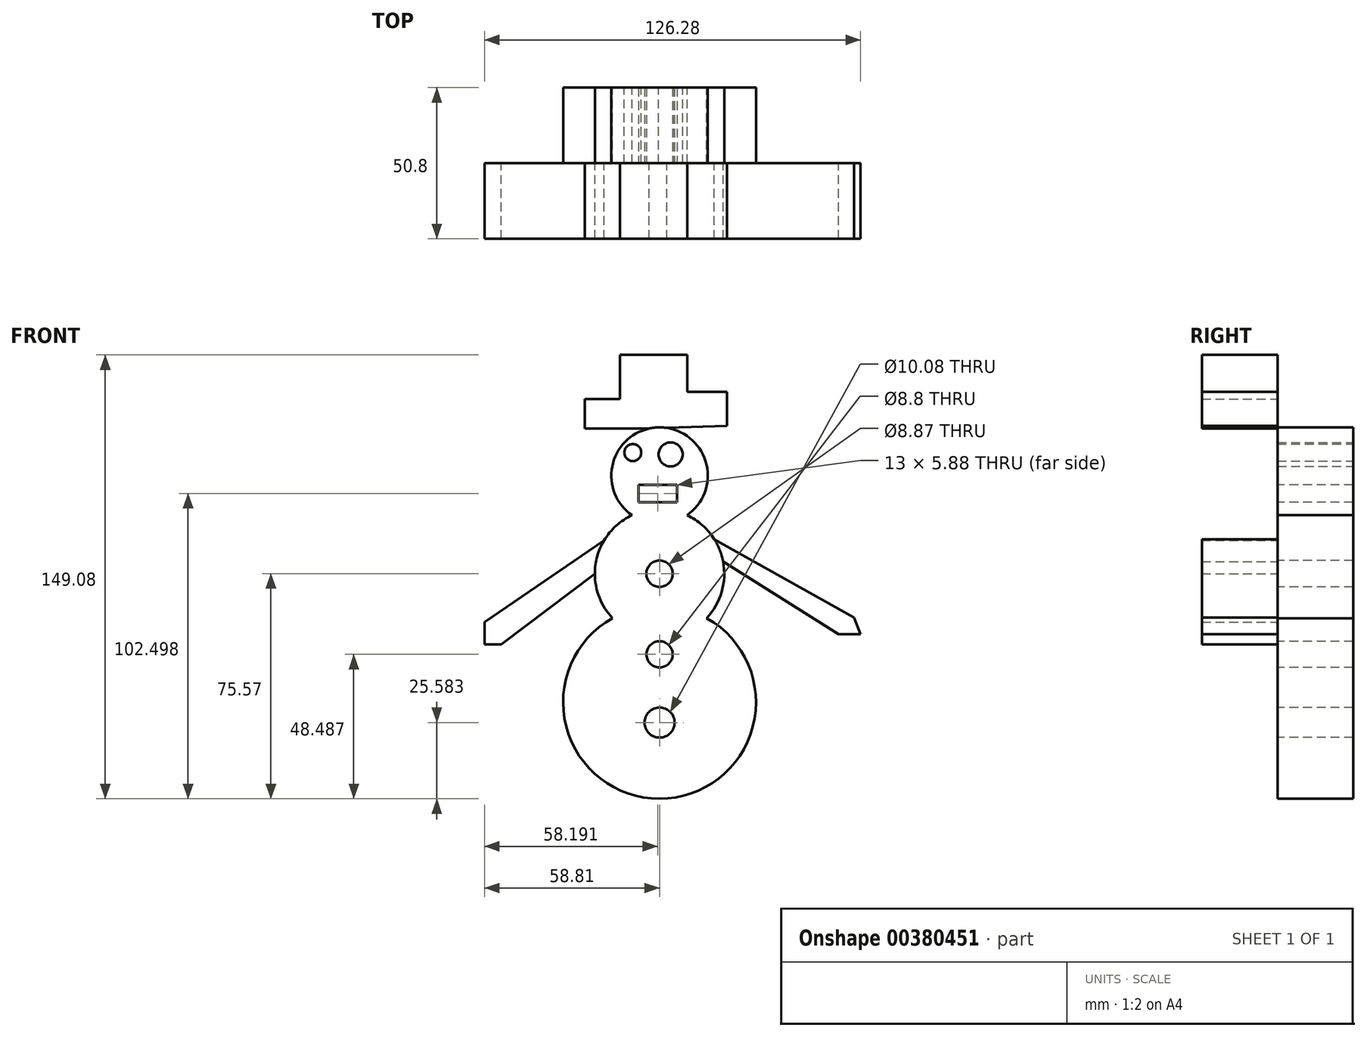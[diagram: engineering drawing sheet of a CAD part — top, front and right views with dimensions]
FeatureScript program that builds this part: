
annotation { "Feature Type Name" : "Feature", "Feature Type Description" : "" }
export const myFeature = defineFeature(function(context is Context, id is Id, definition is map)
    precondition{}
    {
        {
            var Q0;
            Q0=qCreatedBy(makeId("Front.planeOp"),FACE);
            var sketch = newSketch(context, id + "F0", { "sketchPlane" : qUnion([Q0])});
            skCircle(sketch, "E0", {"center": v(0, 0) * mm, "radius": 21.74 * mm});
            skCircle(sketch, "E1", {"center": v(0, -43.18) * mm, "radius": 32.4 * mm});
            skCircle(sketch, "E2", {"center": v(0, 32.96) * mm, "radius": 16.2 * mm});
            skCircle(sketch, "E3", {"center": v(-8.98, 40.7) * mm, "radius": 2.85 * mm});
            skLineSegment(sketch, "E4", {"start": v(-9.9, 28.94) * mm, "end": v(-9.9, 23.37) * mm});
            skLineSegment(sketch, "E5", {"start": v(-9.9, 23.37) * mm, "end": v(8.05, 23.37) * mm});
            skCircle(sketch, "E6", {"center": v(3.71, 40.08) * mm, "radius": 4.04 * mm});
            skLineSegment(sketch, "E7", {"start": v(17.9, 12.33) * mm, "end": v(49.52, -4.49) * mm});
            skLineSegment(sketch, "E8", {"start": v(-18.11, 12.02) * mm, "end": v(-42.4, -4.49) * mm});
            skSolve(sketch);
        }
        {
            var Q0;
            Q0 = qSketchRegion(id + "F0", true);
            extrude(context, id + "F1", {"entities" : qUnion([Q0]), "depth" : 25.4 * mm});
        }
        {
            var Q0;
            Q0=makeQuery(id+"F1.opExtrude","CAP_FACE",FACE,{"disambiguationData":[OSD([sQuery(id+"F0.wireOp",EDGE,"E0"),sQuery(id+"F0.wireOp",EDGE,"E1"),sQuery(id+"F0.wireOp",EDGE,"E2"),sQuery(id+"F0.wireOp",EDGE,"E3"),sQuery(id+"F0.wireOp",EDGE,"E6")])],"isStart":false});
            var sketch = newSketch(context, id + "F2", { "sketchPlane" : qUnion([Q0])});
            skLineSegment(sketch, "E9", {"start": v(-7.12, 29.87) * mm, "end": v(-7.12, 23.99) * mm});
            skLineSegment(sketch, "E10", {"start": v(-7.12, 23.99) * mm, "end": v(5.88, 23.99) * mm});
            skLineSegment(sketch, "E11", {"start": v(5.88, 23.99) * mm, "end": v(5.88, 29.87) * mm});
            skLineSegment(sketch, "E12", {"start": v(5.88, 29.87) * mm, "end": v(-7.12, 29.87) * mm});
            skSolve(sketch);
        }
        {
            var Q0;
            Q0=makeQuery(id+"F2.imprint","IMPRINT",FACE,{"disambiguationData":[TD([[makeQuery(id+"F2.imprint","IMPRINT",EDGE,{"derivedFrom":sQuery(id+"F2.wireOp",EDGE,"E9")}),1.0]])]});
            extrude(context, id + "F3", {"entities" : qUnion([Q0]), "operationType" : NewBodyOperationType.REMOVE, "oppositeDirection" : true, "depth" : 25.4 * mm});
        }
        {
            var Q0;
            Q0=makeQuery(id+"F1.opExtrude","CAP_FACE",FACE,{"disambiguationData":[OSD([sQuery(id+"F0.wireOp",EDGE,"E0"),sQuery(id+"F0.wireOp",EDGE,"E1"),sQuery(id+"F0.wireOp",EDGE,"E2"),sQuery(id+"F0.wireOp",EDGE,"E3"),sQuery(id+"F0.wireOp",EDGE,"E6")])],"isStart":false});
            var sketch = newSketch(context, id + "F4", { "sketchPlane" : qUnion([Q0])});
            skCircle(sketch, "E13", {"center": v(0, 0) * mm, "radius": 4.43 * mm});
            skCircle(sketch, "E14", {"center": v(0, -27.08) * mm, "radius": 4.4 * mm});
            skCircle(sketch, "E15", {"center": v(0, -49.99) * mm, "radius": 5.04 * mm});
            skSolve(sketch);
        }
        {
            var Q0;
            Q0 = qSketchRegion(id + "F4", true);
            extrude(context, id + "F5", {"entities" : qUnion([Q0]), "operationType" : NewBodyOperationType.REMOVE, "oppositeDirection" : true, "depth" : 25.4 * mm});
        }
        {
            var Q0;
            Q0=makeQuery(id+"F1.opExtrude","CAP_FACE",FACE,{"disambiguationData":[OSD([sQuery(id+"F0.wireOp",EDGE,"E0"),sQuery(id+"F0.wireOp",EDGE,"E1"),sQuery(id+"F0.wireOp",EDGE,"E2"),sQuery(id+"F0.wireOp",EDGE,"E3"),sQuery(id+"F0.wireOp",EDGE,"E6")])],"isStart":false});
            var sketch = newSketch(context, id + "F6", { "sketchPlane" : qUnion([Q0])});
            skLineSegment(sketch, "E16", {"start": v(-3.54, 48.77) * mm, "end": v(-25.07, 48.77) * mm});
            skLineSegment(sketch, "E17", {"start": v(-25.07, 48.77) * mm, "end": v(-25.07, 58.65) * mm});
            skLineSegment(sketch, "E18", {"start": v(-25.07, 58.65) * mm, "end": v(-13.3, 58.65) * mm});
            skLineSegment(sketch, "E19", {"start": v(-13.3, 58.65) * mm, "end": v(-13.3, 73.51) * mm});
            skLineSegment(sketch, "E20", {"start": v(-13.3, 73.51) * mm, "end": v(9.25, 73.51) * mm});
            skLineSegment(sketch, "E21", {"start": v(9.25, 73.51) * mm, "end": v(9.25, 61.13) * mm});
            skLineSegment(sketch, "E22", {"start": v(9.25, 61.13) * mm, "end": v(22.6, 61.13) * mm});
            skLineSegment(sketch, "E23", {"start": v(22.6, 61.13) * mm, "end": v(22.6, 49.68) * mm});
            skLineSegment(sketch, "E24", {"start": v(22.6, 49.68) * mm, "end": v(-3.54, 48.77) * mm});
            skSolve(sketch);
        }
        {
            var Q0;
            {var subQ1=sQuery(id+"F6.wireOp",EDGE,"E16");Q0=makeQuery(id+"F6.imprint","IMPRINT",FACE,{"disambiguationData":[TD([[makeQuery(id+"F6.imprint","IMPRINT",EDGE,{"derivedFrom":subQ1}),-1.0]])]});}
            extrude(context, id + "F7", {"entities" : qUnion([Q0]), "depth" : 25.4 * mm});
        }
        {
            var Q0;
            Q0=makeQuery(id+"F1.opExtrude","CAP_FACE",FACE,{"disambiguationData":[OSD([sQuery(id+"F0.wireOp",EDGE,"E0"),sQuery(id+"F0.wireOp",EDGE,"E1"),sQuery(id+"F0.wireOp",EDGE,"E2"),sQuery(id+"F0.wireOp",EDGE,"E3"),sQuery(id+"F0.wireOp",EDGE,"E6")])],"isStart":false});
            var sketch = newSketch(context, id + "F8", { "sketchPlane" : qUnion([Q0])});
            skLineSegment(sketch, "E25", {"start": v(18.39, 11.6) * mm, "end": v(65.3, -14.7) * mm});
            skLineSegment(sketch, "E26", {"start": v(65.3, -14.7) * mm, "end": v(67.47, -20.27) * mm});
            skLineSegment(sketch, "E27", {"start": v(67.47, -20.27) * mm, "end": v(60.05, -20.27) * mm});
            skLineSegment(sketch, "E28", {"start": v(60.05, -20.27) * mm, "end": v(21.36, 4.05) * mm});
            skLineSegment(sketch, "E29", {"start": v(21.36, 4.05) * mm, "end": v(18.39, 11.6) * mm});
            skSolve(sketch);
        }
        {
            var Q0;
            {var subQ1=sQuery(id+"F8.wireOp",EDGE,"E25");Q0=makeQuery(id+"F8.imprint","IMPRINT",FACE,{"disambiguationData":[TD([[makeQuery(id+"F8.imprint","IMPRINT",EDGE,{"derivedFrom":subQ1}),-1.0]])]});}
            extrude(context, id + "F9", {"entities" : qUnion([Q0]), "depth" : 25.4 * mm});
        }
        {
            var Q0;
            Q0=makeQuery(id+"F1.opExtrude","CAP_FACE",FACE,{"disambiguationData":[OSD([sQuery(id+"F0.wireOp",EDGE,"E0"),sQuery(id+"F0.wireOp",EDGE,"E1"),sQuery(id+"F0.wireOp",EDGE,"E2"),sQuery(id+"F0.wireOp",EDGE,"E3"),sQuery(id+"F0.wireOp",EDGE,"E6")])],"isStart":false});
            var sketch = newSketch(context, id + "F10", { "sketchPlane" : qUnion([Q0])});
            skLineSegment(sketch, "E30", {"start": v(-18.65, 11.17) * mm, "end": v(-58.8, -16.25) * mm});
            skLineSegment(sketch, "E31", {"start": v(-58.8, -16.25) * mm, "end": v(-58.8, -23.68) * mm});
            skLineSegment(sketch, "E32", {"start": v(-58.8, -23.68) * mm, "end": v(-53.24, -23.68) * mm});
            skLineSegment(sketch, "E33", {"start": v(-53.24, -23.68) * mm, "end": v(-21.74, 0) * mm});
            skLineSegment(sketch, "E34", {"start": v(-21.74, 0) * mm, "end": v(-18.65, 11.17) * mm});
            skSolve(sketch);
        }
        {
            var Q0;
            {var subQ1=sQuery(id+"F10.wireOp",EDGE,"E30");Q0=makeQuery(id+"F10.imprint","IMPRINT",FACE,{"disambiguationData":[TD([[makeQuery(id+"F10.imprint","IMPRINT",EDGE,{"derivedFrom":subQ1}),1.0]])]});}
            extrude(context, id + "F11", {"entities" : qUnion([Q0]), "depth" : 25.4 * mm});
        }
    });
